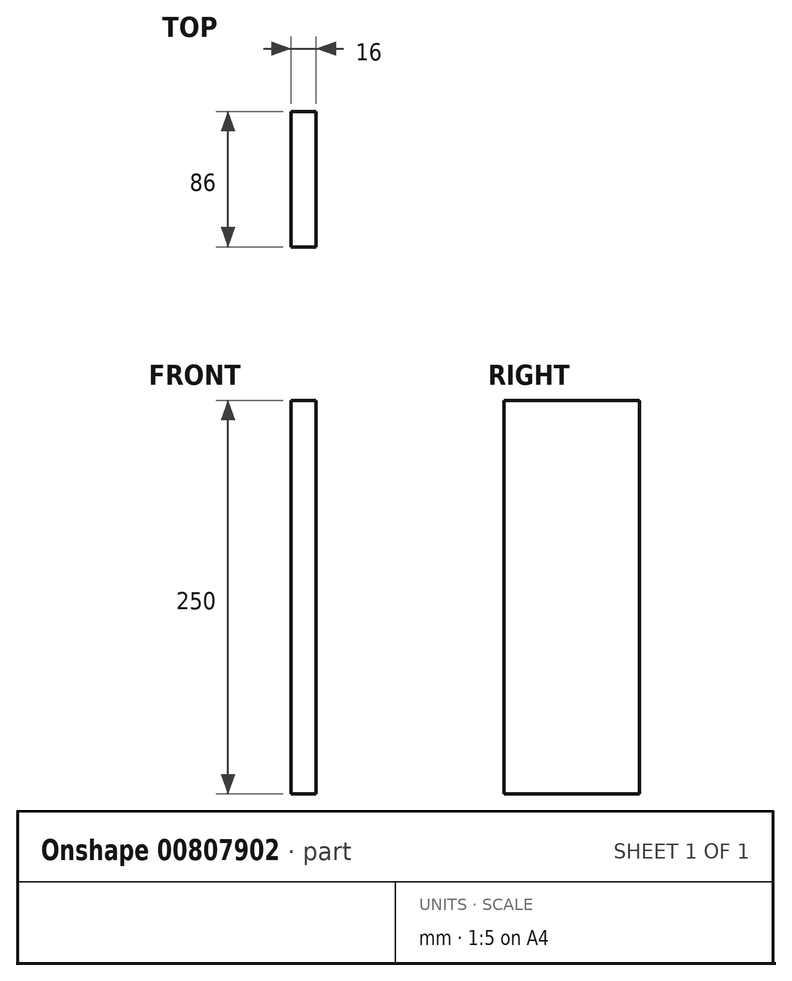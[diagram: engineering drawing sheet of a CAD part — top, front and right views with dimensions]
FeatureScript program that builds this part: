
annotation { "Feature Type Name" : "Feature", "Feature Type Description" : "" }
export const myFeature = defineFeature(function(context is Context, id is Id, definition is map)
    precondition{}
    {
        {
            var Q0;
            Q0=qCreatedBy(makeId("Top.planeOp"),FACE);
            var sketch = newSketch(context, id + "F0", { "sketchPlane" : qUnion([Q0])});
            skLineSegment(sketch, "E0.bottom", {"start": v(0, 0) * mm, "end": v(16, 0) * mm});
            skLineSegment(sketch, "E0.top", {"start": v(0, 86) * mm, "end": v(16, 86) * mm});
            skLineSegment(sketch, "E0.left", {"start": v(0, 0) * mm, "end": v(0, 86) * mm});
            skLineSegment(sketch, "E0.right", {"start": v(16, 0) * mm, "end": v(16, 86) * mm});
            skSolve(sketch);
        }
        {
            var Q0;
            Q0 = qSketchRegion(id + "F0", true);
            extrude(context, id + "F1", {"entities" : qUnion([Q0]), "depth" : 250 * mm, "offsetDistance" : 25 * mm});
        }
    });
